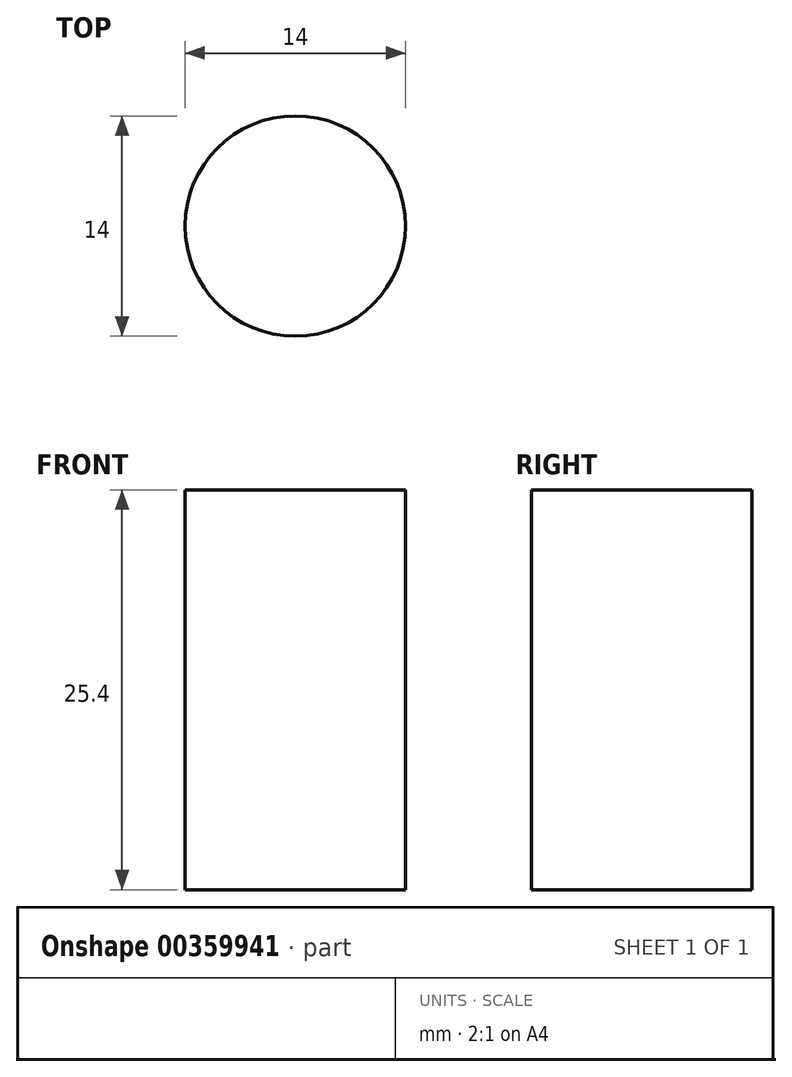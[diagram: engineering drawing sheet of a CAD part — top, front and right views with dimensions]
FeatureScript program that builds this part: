
annotation { "Feature Type Name" : "Feature", "Feature Type Description" : "" }
export const myFeature = defineFeature(function(context is Context, id is Id, definition is map)
    precondition{}
    {
        {
            var Q0;
            Q0=qCreatedBy(makeId("Top.planeOp"),FACE);
            var sketch = newSketch(context, id + "F0", { "sketchPlane" : qUnion([Q0])});
            skCircle(sketch, "E0", {"center": v(0, -2.17) * mm, "radius": 7 * mm});
            skSolve(sketch);
        }
        {
            var Q0;
            Q0 = qSketchRegion(id + "F0", true);
            extrude(context, id + "F1", {"entities" : qUnion([Q0]), "depth" : 25.4 * mm});
        }
    });
